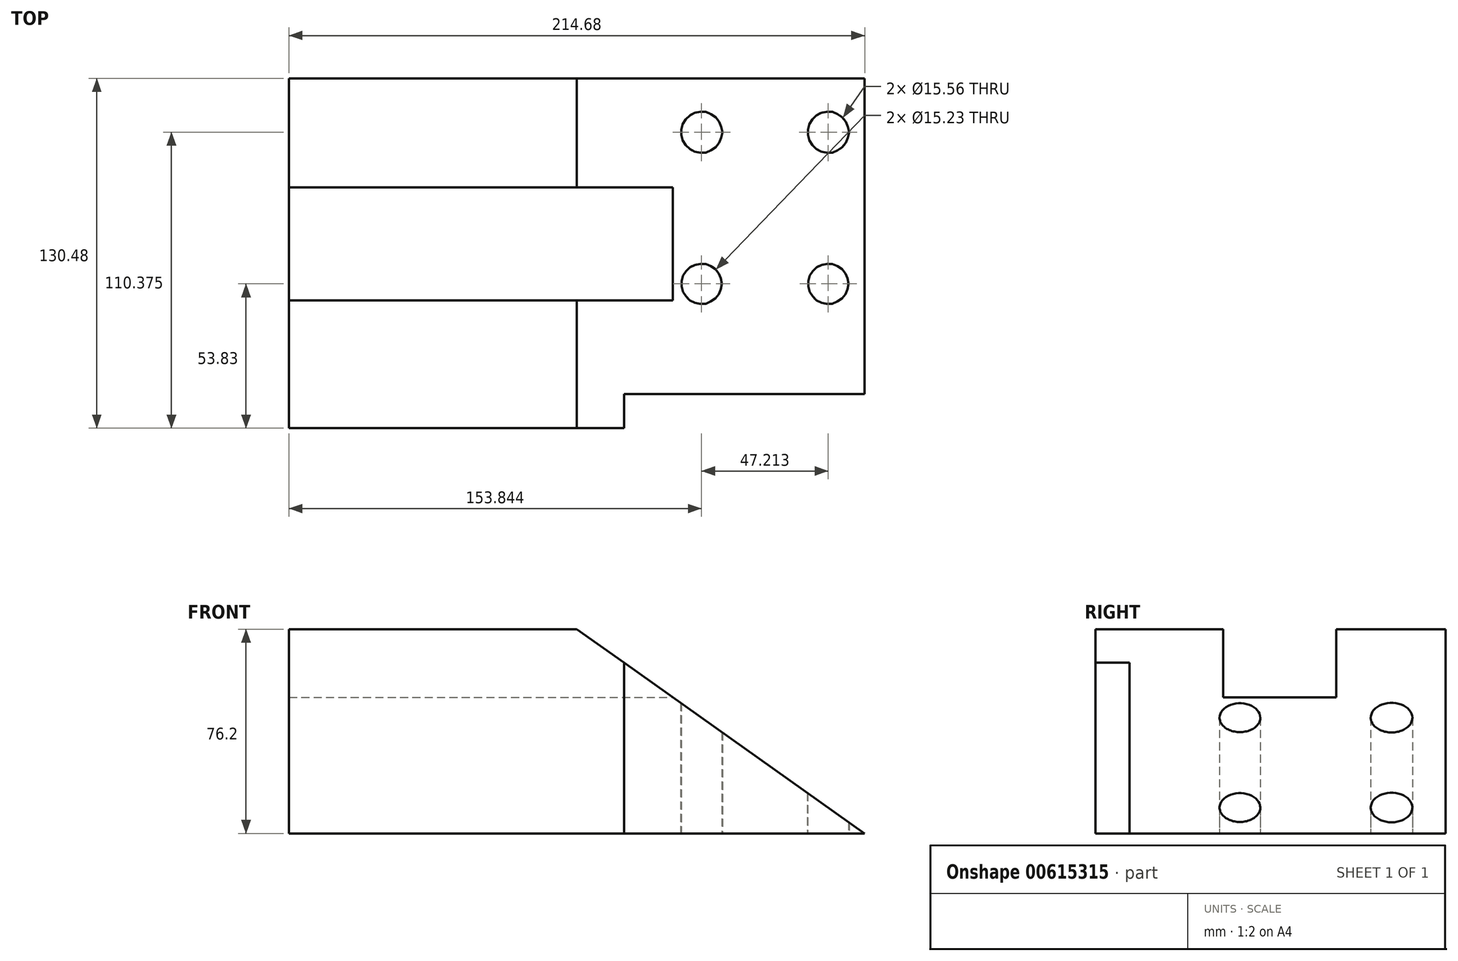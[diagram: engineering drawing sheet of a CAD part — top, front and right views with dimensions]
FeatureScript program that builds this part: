
annotation { "Feature Type Name" : "Feature", "Feature Type Description" : "" }
export const myFeature = defineFeature(function(context is Context, id is Id, definition is map)
    precondition{}
    {
        {
            var Q0;
            Q0=qCreatedBy(makeId("Top.planeOp"),FACE);
            var sketch = newSketch(context, id + "F0", { "sketchPlane" : qUnion([Q0])});
            skLineSegment(sketch, "E0.bottom", {"start": v(107.34, -65.24) * mm, "end": v(-107.34, -65.24) * mm});
            skLineSegment(sketch, "E0.top", {"start": v(107.34, 65.24) * mm, "end": v(-107.34, 65.24) * mm});
            skLineSegment(sketch, "E0.left", {"start": v(107.34, -65.24) * mm, "end": v(107.34, 65.24) * mm});
            skLineSegment(sketch, "E0.right", {"start": v(-107.34, -65.24) * mm, "end": v(-107.34, 65.24) * mm});
            skPoint(sketch, "E0.middle", {"position": v(0, 0) * mm});
            skSolve(sketch);
        }
        {
            var Q0;
            Q0=makeQuery(id+"F0.imprint","IMPRINT",FACE,{"disambiguationData":[TD([[makeQuery(id+"F0.imprint","IMPRINT",EDGE,{"derivedFrom":sQuery(id+"F0.wireOp",EDGE,"E0.bottom")}),-1.0]])]});
            extrude(context, id + "F1", {"entities" : qUnion([Q0]), "depth" : 76.2 * mm, "offsetDistance" : 25.4 * mm});
        }
        {
            var Q0;
            Q0=makeQuery(id+"F1.opExtrude","SWEPT_FACE",FACE,{"disambiguationData":[OSD([sQuery(id+"F0.wireOp",EDGE,"E0.bottom")])]});
            var sketch = newSketch(context, id + "F2", { "sketchPlane" : qUnion([Q0])});
            skLineSegment(sketch, "E1", {"start": v(0, 76.2) * mm, "end": v(107.34, 76.2) * mm});
            skLineSegment(sketch, "E2", {"start": v(107.34, 76.2) * mm, "end": v(107.34, 0) * mm});
            skLineSegment(sketch, "E3", {"start": v(107.34, 0) * mm, "end": v(0, 76.2) * mm});
            skSolve(sketch);
        }
        {
            var Q0;
            Q0 = qSketchRegion(id + "F2", true);
            extrude(context, id + "F3", {"entities" : qUnion([Q0]), "operationType" : NewBodyOperationType.REMOVE, "oppositeDirection" : true, "depth" : 2540 * mm, "offsetDistance" : 25.4 * mm});
        }
        {
            var Q0;
            Q0=makeQuery(id+"F1.opExtrude","CAP_FACE",FACE,{"disambiguationData":[OSD([sQuery(id+"F0.wireOp",EDGE,"E0.bottom"),sQuery(id+"F0.wireOp",EDGE,"E0.top"),sQuery(id+"F0.wireOp",EDGE,"E0.left"),sQuery(id+"F0.wireOp",EDGE,"E0.right")])],"isStart":false});
            var sketch = newSketch(context, id + "F4", { "sketchPlane" : qUnion([Q0])});
            skLineSegment(sketch, "E4", {"start": v(-107.34, 24.56) * mm, "end": v(0, 24.56) * mm});
            skLineSegment(sketch, "E5", {"start": v(0, 24.56) * mm, "end": v(0, -17.6) * mm});
            skLineSegment(sketch, "E6", {"start": v(0, -17.6) * mm, "end": v(-107.34, -17.6) * mm});
            skLineSegment(sketch, "E7", {"start": v(-107.34, -17.6) * mm, "end": v(-107.34, 24.56) * mm});
            skSolve(sketch);
        }
        {
            var Q0;
            Q0 = qSketchRegion(id + "F4", true);
            extrude(context, id + "F5", {"entities" : qUnion([Q0]), "operationType" : NewBodyOperationType.REMOVE, "oppositeDirection" : true, "depth" : 25.4 * mm, "offsetDistance" : 25.4 * mm});
        }
        {
            var Q0;
            Q0=makeQuery(id+"F5.boolean.opBoolean","COPY",FACE,{"derivedFrom":makeQuery(id+"F5.opExtrude","SWEPT_FACE",FACE,{"disambiguationData":[OSD([sQuery(id+"F4.wireOp",EDGE,"E5")])]})});
            var sketch = newSketch(context, id + "F6", { "sketchPlane" : qUnion([Q0])});
            skLineSegment(sketch, "E8", {"start": v(-24.56, 76.2) * mm, "end": v(-24.56, 50.8) * mm});
            skLineSegment(sketch, "E9", {"start": v(-24.56, 50.8) * mm, "end": v(17.6, 50.8) * mm});
            skLineSegment(sketch, "E10", {"start": v(17.6, 50.8) * mm, "end": v(17.6, 76.2) * mm});
            skLineSegment(sketch, "E11", {"start": v(17.6, 76.2) * mm, "end": v(-24.56, 76.2) * mm});
            skSolve(sketch);
        }
        {
            var Q0;
            Q0 = qSketchRegion(id + "F6", true);
            extrude(context, id + "F7", {"entities" : qUnion([Q0]), "operationType" : NewBodyOperationType.REMOVE, "oppositeDirection" : true, "depth" : 25.4 * mm, "offsetDistance" : 25.4 * mm});
        }
        {
            var Q0;
            Q0=makeQuery(id+"F7.boolean.opBoolean","COPY",FACE,{"derivedFrom":makeQuery(id+"F7.opExtrude","CAP_FACE",FACE,{"disambiguationData":[OSD([sQuery(id+"F6.wireOp",EDGE,"E8"),sQuery(id+"F6.wireOp",EDGE,"E9"),sQuery(id+"F6.wireOp",EDGE,"E10"),sQuery(id+"F6.wireOp",EDGE,"E11")])],"isStart":false})});
            extrude(context, id + "F8", {"entities" : qUnion([Q0]), "operationType" : NewBodyOperationType.REMOVE, "oppositeDirection" : true, "depth" : 25.4 * mm, "offsetDistance" : 25.4 * mm});
        }
        {
            var Q0;
            Q0=makeQuery(id+"F1.opExtrude","SWEPT_FACE",FACE,{"disambiguationData":[OSD([sQuery(id+"F0.wireOp",EDGE,"E0.bottom")])]});
            var sketch = newSketch(context, id + "F9", { "sketchPlane" : qUnion([Q0])});
            skLineSegment(sketch, "E12", {"start": v(17.63, 63.68) * mm, "end": v(17.63, 0) * mm});
            skLineSegment(sketch, "E13", {"start": v(17.63, 0) * mm, "end": v(107.34, 0) * mm});
            skLineSegment(sketch, "E14", {"start": v(107.34, 0) * mm, "end": v(17.63, 63.68) * mm});
            skSolve(sketch);
        }
        {
            var Q0;
            Q0 = qSketchRegion(id + "F9", true);
            extrude(context, id + "F10", {"entities" : qUnion([Q0]), "operationType" : NewBodyOperationType.REMOVE, "oppositeDirection" : true, "depth" : 12.7 * mm, "offsetDistance" : 25.4 * mm});
        }
        {
            var Q0;
            Q0=qCreatedBy(makeId("Top.planeOp"),FACE);
            var sketch = newSketch(context, id + "F11", { "sketchPlane" : qUnion([Q0])});
            skCircle(sketch, "E15", {"center": v(46.5, 45.14) * mm, "radius": 7.78 * mm});
            skCircle(sketch, "E16", {"center": v(46.5, -11.4) * mm, "radius": 7.61 * mm});
            skCircle(sketch, "E17", {"center": v(93.72, -11.4) * mm, "radius": 7.61 * mm});
            skCircle(sketch, "E18", {"center": v(93.72, 45.14) * mm, "radius": 7.78 * mm});
            skSolve(sketch);
        }
        {
            var Q0;
            Q0 = qSketchRegion(id + "F11", true);
            extrude(context, id + "F12", {"entities" : qUnion([Q0]), "operationType" : NewBodyOperationType.REMOVE, "endBound" : BoundingType.THROUGH_ALL, "depth" : 25.4 * mm, "offsetDistance" : 25.4 * mm});
        }
    });
